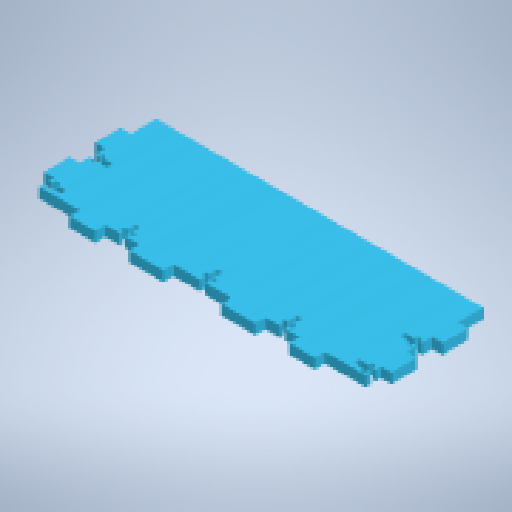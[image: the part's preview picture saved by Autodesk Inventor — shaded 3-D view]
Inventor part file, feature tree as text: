
AUTODESK INVENTOR PART (.ipt)
format: ipt  version: 2024.2 (Build 282272000, 272)  size: 337,920 bytes
history: native  units: mm
features: extrude x2, sketch x2, other x1
ambient origin geometry x8: Origin, YZ Plane, XZ Plane, XY Plane, X Axis, Y Axis, Z Axis, Center Point
bodies: Body1 (feature_tree)
feature tree (5):
  other  "Твердое тело1"
  extrude  "Выдавливание1"  Depth=204.0mm
  extrude  "Выдавливание2"  Depth=60.0mm
  sketch  "Эскиз1"
  sketch  "Эскиз2"
